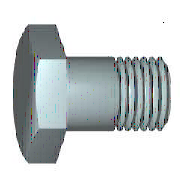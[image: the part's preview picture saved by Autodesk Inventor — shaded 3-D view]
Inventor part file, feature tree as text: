
AUTODESK INVENTOR PART (.ipt)
format: ipt  version: 2022 (Build 260153000, 153)  size: 198,656 bytes
history: native  units: mm (DEFAULTED — no unit token found)
features: sketch x3, other x1, extrude x1, chamfer x1, plane x1
ambient origin geometry x7: Origin, YZ Plane, XZ Plane, X Axis, Y Axis, Z Axis, Center Point
bodies: Solid1 (feature_tree)
feature tree (7):
  other  "Cuerpo"
  extrude  "Cabeza"  Depth=10.0mm
  chamfer  "Chaflán1"  Distance=3.0mm
  plane  "Work Plane1"
  sketch  "Boceto1"  dims[d0=10.0mm d1=7.6mm]
  sketch  "Boceto2"  dims[d2=5.0mm]
  sketch  "Boceto4"  dims[d12=90.0deg d3=3.0mm d4=0.0mm d5=30.0deg d21=90.0deg d6=0.49076mm d7=0.49086mm d8=0.0mm d9=0.5001mm d10=8.0mm d11=8.0mm d13=0.49086mm d14=5.0mm d15=7.6mm d16=0.0mm d19=8.0mm d55=45.0deg d57=0.0mm d58=0.0mm]
